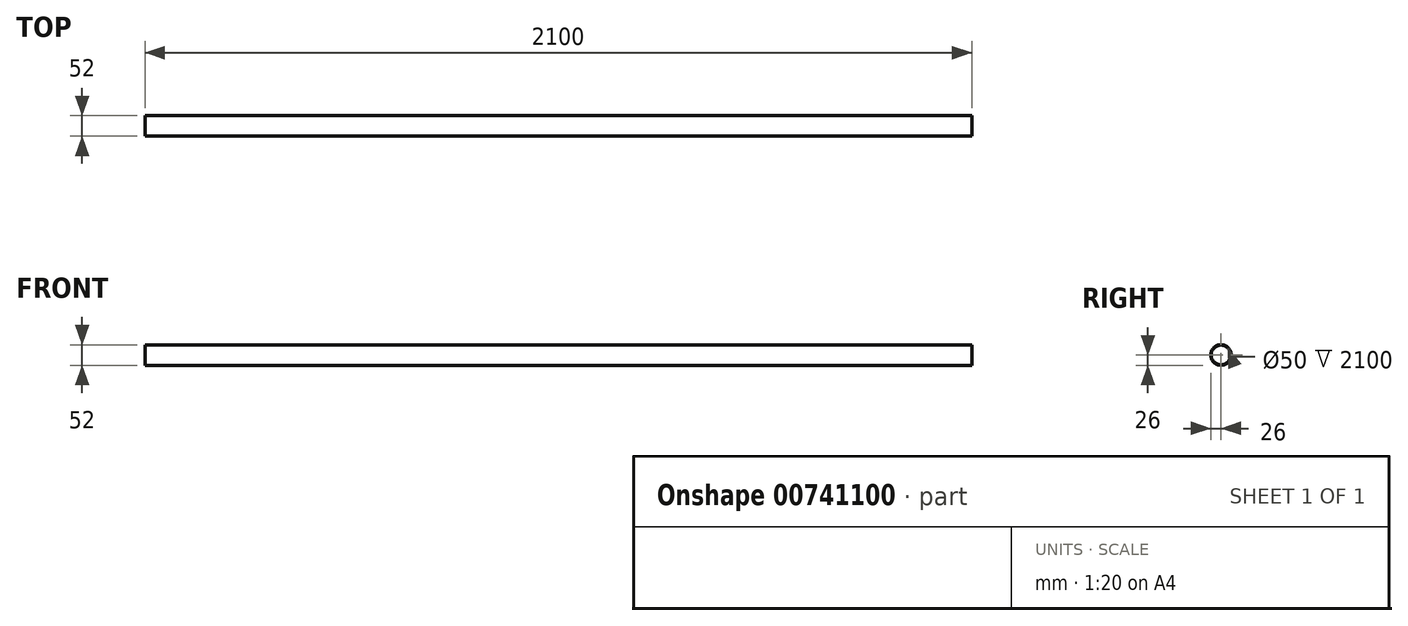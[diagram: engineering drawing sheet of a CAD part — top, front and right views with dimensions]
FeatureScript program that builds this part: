
annotation { "Feature Type Name" : "Feature", "Feature Type Description" : "" }
export const myFeature = defineFeature(function(context is Context, id is Id, definition is map)
    precondition{}
    {
        {
            var Q0;
            Q0=qCreatedBy(makeId("Right.planeOp"),FACE);
            var sketch = newSketch(context, id + "F0", { "sketchPlane" : qUnion([Q0])});
            skCircle(sketch, "E0", {"center": v(0, 0) * mm, "radius": 26 * mm});
            skCircle(sketch, "E1", {"center": v(0, 0) * mm, "radius": 25 * mm});
            skSolve(sketch);
        }
        {
            var Q0;
            Q0=qSketchRegion(id+"F0",true);
            extrude(context, id + "F1", {"entities" : qUnion([Q0]), "endBound" : BoundingType.SYMMETRIC, "depth" : 2100 * mm, "offsetDistance" : 25 * mm});
        }
    });
